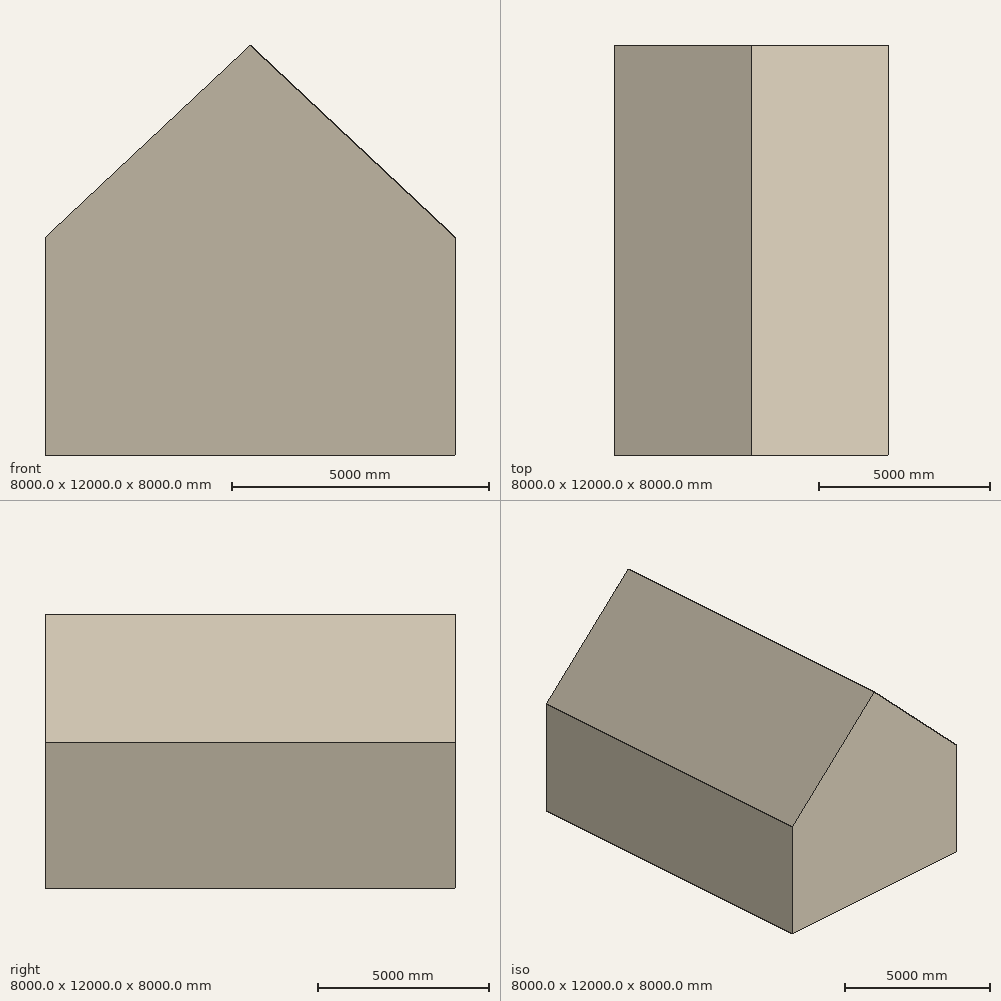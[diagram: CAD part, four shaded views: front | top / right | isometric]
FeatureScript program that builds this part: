
annotation { "Feature Type Name" : "Feature", "Feature Type Description" : "" }
export const myFeature = defineFeature(function(context is Context, id is Id, definition is map)
    precondition{}
    {
        {
            var Q0;
            Q0=qCreatedBy(makeId("Front.planeOp"),FACE);
            var sketch = newSketch(context, id + "F0", { "sketchPlane" : qUnion([Q0])});
            skLineSegment(sketch, "E0", {"start": v(0, 0) * mm, "end": v(0, 4252.25) * mm});
            skLineSegment(sketch, "E1", {"start": v(0, 0) * mm, "end": v(0, 8000) * mm});
            skLineSegment(sketch, "E2", {"start": v(0, 0) * mm, "end": v(8000, 0) * mm});
            skLineSegment(sketch, "E3", {"start": v(8000, 0) * mm, "end": v(8000, 8000) * mm});
            skLineSegment(sketch, "E4", {"start": v(0, 0) * mm, "end": v(4000, 0) * mm});
            skLineSegment(sketch, "E5", {"start": v(4000, 8000) * mm, "end": v(0, 4252.25) * mm});
            skLineSegment(sketch, "E6", {"start": v(4000, 8000) * mm, "end": v(8000, 4252.25) * mm});
            skSolve(sketch);
        }
        {
            var Q0;
            Q0 = qSketchRegion(id + "F0", true);
            extrude(context, id + "F1", {"entities" : qUnion([Q0]), "depth" : 12000 * mm});
        }
    });
